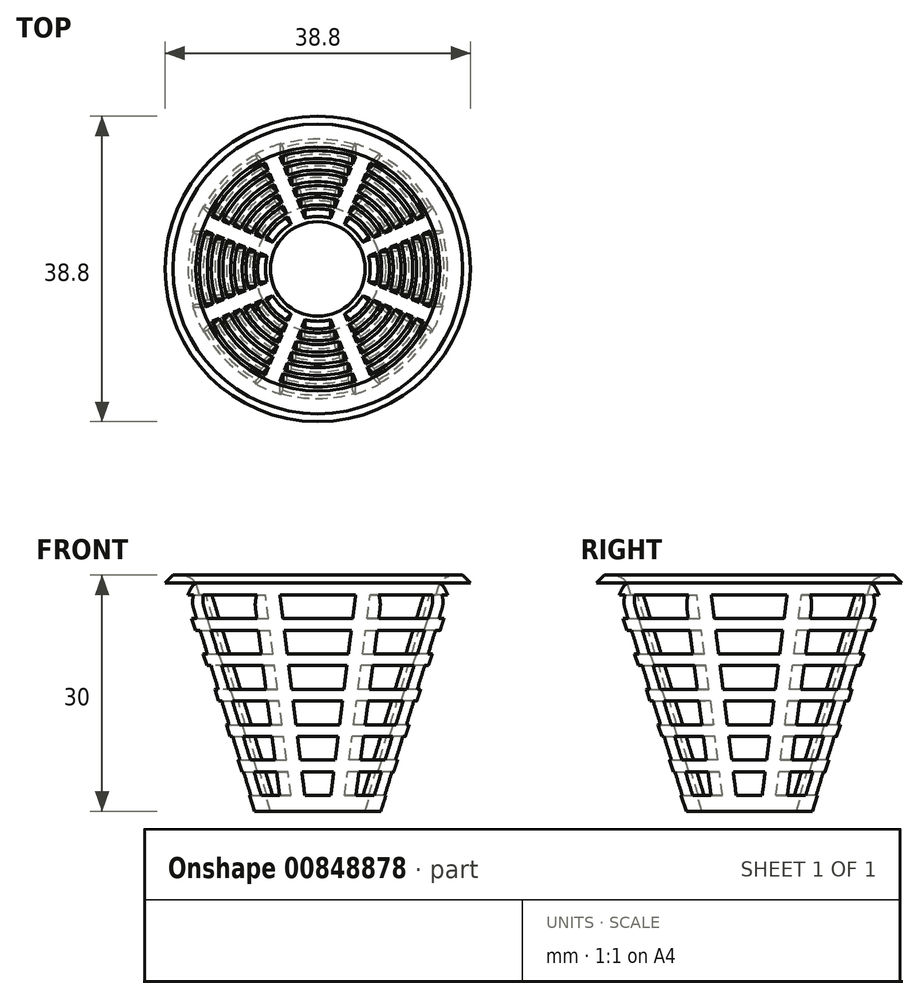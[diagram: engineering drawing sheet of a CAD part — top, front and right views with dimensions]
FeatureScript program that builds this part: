
annotation { "Feature Type Name" : "Feature", "Feature Type Description" : "" }
export const myFeature = defineFeature(function(context is Context, id is Id, definition is map)
    precondition{}
    {
        {
            var Q0;
            Q0=qCreatedBy(makeId("Top.planeOp"),FACE);
            var sketch = newSketch(context, id + "F0", { "sketchPlane" : qUnion([Q0])});
            skCircle(sketch, "E0", {"center": v(0, 0) * mm, "radius": 20 * mm});
            skCircle(sketch, "E1", {"center": v(0, 0) * mm, "radius": 24 * mm});
            skCircle(sketch, "E2", {"center": v(0, 0) * mm, "radius": 21 * mm});
            skCircle(sketch, "E3", {"center": v(0, 24) * mm, "radius": 1 * mm});
            skCircle(sketch, "E4.1.0", {"center": v(-3.75, 23.7) * mm, "radius": 1 * mm});
            skCircle(sketch, "E4.2.0", {"center": v(-7.42, 22.83) * mm, "radius": 1 * mm});
            skCircle(sketch, "E4.3.0", {"center": v(-10.9, 21.38) * mm, "radius": 1 * mm});
            skCircle(sketch, "E4.4.0", {"center": v(-14.1, 19.42) * mm, "radius": 1 * mm});
            skCircle(sketch, "E4.5.0", {"center": v(-16.97, 16.97) * mm, "radius": 1 * mm});
            skCircle(sketch, "E4.6.0", {"center": v(-19.42, 14.1) * mm, "radius": 1 * mm});
            skCircle(sketch, "E4.7.0", {"center": v(-21.38, 10.9) * mm, "radius": 1 * mm});
            skCircle(sketch, "E4.8.0", {"center": v(-22.83, 7.42) * mm, "radius": 1 * mm});
            skCircle(sketch, "E4.9.0", {"center": v(-23.7, 3.75) * mm, "radius": 1 * mm});
            skCircle(sketch, "E4.10.0", {"center": v(-24, 0) * mm, "radius": 1 * mm});
            skCircle(sketch, "E4.11.0", {"center": v(-23.7, -3.75) * mm, "radius": 1 * mm});
            skCircle(sketch, "E4.12.0", {"center": v(-22.83, -7.42) * mm, "radius": 1 * mm});
            skCircle(sketch, "E4.13.0", {"center": v(-21.38, -10.9) * mm, "radius": 1 * mm});
            skCircle(sketch, "E4.14.0", {"center": v(-19.42, -14.1) * mm, "radius": 1 * mm});
            skCircle(sketch, "E4.15.0", {"center": v(-16.97, -16.97) * mm, "radius": 1 * mm});
            skCircle(sketch, "E4.16.0", {"center": v(-14.1, -19.42) * mm, "radius": 1 * mm});
            skCircle(sketch, "E4.17.0", {"center": v(-10.9, -21.38) * mm, "radius": 1 * mm});
            skCircle(sketch, "E4.18.0", {"center": v(-7.42, -22.83) * mm, "radius": 1 * mm});
            skCircle(sketch, "E4.19.0", {"center": v(-3.75, -23.7) * mm, "radius": 1 * mm});
            skCircle(sketch, "E4.20.0", {"center": v(0, -24) * mm, "radius": 1 * mm});
            skCircle(sketch, "E4.21.0", {"center": v(3.75, -23.7) * mm, "radius": 1 * mm});
            skCircle(sketch, "E4.22.0", {"center": v(7.42, -22.83) * mm, "radius": 1 * mm});
            skCircle(sketch, "E4.23.0", {"center": v(10.9, -21.38) * mm, "radius": 1 * mm});
            skCircle(sketch, "E4.24.0", {"center": v(14.1, -19.42) * mm, "radius": 1 * mm});
            skCircle(sketch, "E4.25.0", {"center": v(16.97, -16.97) * mm, "radius": 1 * mm});
            skCircle(sketch, "E4.26.0", {"center": v(19.42, -14.1) * mm, "radius": 1 * mm});
            skCircle(sketch, "E4.27.0", {"center": v(21.38, -10.9) * mm, "radius": 1 * mm});
            skCircle(sketch, "E4.28.0", {"center": v(22.83, -7.42) * mm, "radius": 1 * mm});
            skCircle(sketch, "E4.29.0", {"center": v(23.7, -3.75) * mm, "radius": 1 * mm});
            skCircle(sketch, "E4.30.0", {"center": v(24, 0) * mm, "radius": 1 * mm});
            skCircle(sketch, "E4.31.0", {"center": v(23.7, 3.75) * mm, "radius": 1 * mm});
            skCircle(sketch, "E4.32.0", {"center": v(22.83, 7.42) * mm, "radius": 1 * mm});
            skCircle(sketch, "E4.33.0", {"center": v(21.38, 10.9) * mm, "radius": 1 * mm});
            skCircle(sketch, "E4.34.0", {"center": v(19.42, 14.1) * mm, "radius": 1 * mm});
            skCircle(sketch, "E4.35.0", {"center": v(16.97, 16.97) * mm, "radius": 1 * mm});
            skCircle(sketch, "E4.36.0", {"center": v(14.1, 19.42) * mm, "radius": 1 * mm});
            skCircle(sketch, "E4.37.0", {"center": v(10.9, 21.38) * mm, "radius": 1 * mm});
            skCircle(sketch, "E4.38.0", {"center": v(7.42, 22.83) * mm, "radius": 1 * mm});
            skCircle(sketch, "E4.39.0", {"center": v(3.75, 23.7) * mm, "radius": 1 * mm});
            skCircle(sketch, "E5", {"center": v(0, 0) * mm, "radius": 15.5 * mm});
            skCircle(sketch, "E6", {"center": v(0, 0) * mm, "radius": 17.5 * mm});
            skCircle(sketch, "E7", {"center": v(0, 0) * mm, "radius": 19.5 * mm});
            skSolve(sketch);
        }
        {
            var Q0;
            Q0=makeQuery(id+"F0.imprint","IMPRINT",FACE,{"disambiguationData":[TD([[makeQuery(id+"F0.imprint","IMPRINT",EDGE,{"derivedFrom":sQuery(id+"F0.wireOp",EDGE,"E6")}),-1.0]])]});
            var Q1;
            Q1=makeQuery(id+"F0.imprint","IMPRINT",FACE,{"disambiguationData":[TD([[makeQuery(id+"F0.imprint","IMPRINT",EDGE,{"derivedFrom":sQuery(id+"F0.wireOp",EDGE,"E5")}),-1.0]])]});
            extrude(context, id + "F1", {"entities" : qUnion([Q0, Q1]), "oppositeDirection" : true, "depth" : 1 * mm, "offsetDistance" : 25 * mm});
        }
        {
            var Q0;
            Q0=qCreatedBy(makeId("Top.planeOp"),FACE);
            cPlane(context, id + "F2", {"entities" : qUnion([Q0]), "cplaneType" : CPlaneType.OFFSET, "offset" : 30 * mm, "oppositeDirection" : true, "width" : 150 * mm, "height" : 150 * mm});
        }
        {
            var Q0;
            Q0=qCreatedBy(makeId("Front.planeOp"),FACE);
            var sketch = newSketch(context, id + "F3", { "sketchPlane" : qUnion([Q0])});
            skLineSegment(sketch, "E8", {"start": v(-8, -30) * mm, "end": v(-17.5, -1) * mm});
            skLineSegment(sketch, "E9", {"start": v(-17.5, -1) * mm, "end": v(-15.5, -1) * mm});
            skLineSegment(sketch, "E10", {"start": v(-15.5, -1) * mm, "end": v(-6, -30) * mm});
            skLineSegment(sketch, "E11", {"start": v(-6, -30) * mm, "end": v(-8, -30) * mm});
            skLineSegment(sketch, "E12", {"start": v(0, 0) * mm, "end": v(0, -30) * mm, "construction": true});
            skSolve(sketch);
        }
        {
            var Q0;
            Q0=makeQuery(id+"F3.imprint","IMPRINT",FACE,{"disambiguationData":[TD([[makeQuery(id+"F3.imprint","IMPRINT",EDGE,{"derivedFrom":sQuery(id+"F3.wireOp",EDGE,"E8")}),-1.0]])]});
            var Q1;
            Q1=sQuery(id+"F3.wireOp",EDGE,"E12");
            revolve(context, id + "F4", {"surfaceOperationType" : NewSurfaceOperationType.NEW, "entities" : qUnion([Q0]), "axis" : qUnion([Q1]), "revolveType" : RevolveType.FULL});
        }
        {
            var Q0;
            Q0=makeQuery(id+"F1.opExtrude","CAP_EDGE",EDGE,{"disambiguationData":[OSD([sQuery(id+"F0.wireOp",EDGE,"E5")])],"isStart":true});
            fillet(context, id + "F5", {"entities" : qUnion([Q0]), "radius" : 2.5 * mm, "tangentPropagation" : true, "allowEdgeOverflow" : false});
        }
        {
            var Q0;
            Q0=qCreatedBy(makeId("Front.planeOp"),FACE);
            var sketch = newSketch(context, id + "F6", { "sketchPlane" : qUnion([Q0])});
            skLineSegment(sketch, "E13", {"start": v(0, -30) * mm, "end": v(-1.4, -30) * mm});
            skLineSegment(sketch, "E14", {"start": v(0, -1) * mm, "end": v(-5, -1) * mm});
            skLineSegment(sketch, "E15", {"start": v(-5, -1) * mm, "end": v(-1.4, -30) * mm});
            skLineSegment(sketch, "E16.MirrorCS", {"start": v(5, -1) * mm, "end": v(1.4, -30) * mm});
            skLineSegment(sketch, "E17.MirrorCS", {"start": v(0, -1) * mm, "end": v(5, -1) * mm});
            skLineSegment(sketch, "E18.MirrorCS", {"start": v(0, -30) * mm, "end": v(1.4, -30) * mm});
            skLineSegment(sketch, "E19", {"start": v(-4.81, -2.5) * mm, "end": v(4.81, -2.5) * mm});
            skLineSegment(sketch, "E20.0.1.0", {"start": v(-4.63, -4) * mm, "end": v(4.63, -4) * mm});
            skLineSegment(sketch, "E20.0.2.0", {"start": v(-4.44, -5.5) * mm, "end": v(4.44, -5.5) * mm});
            skLineSegment(sketch, "E20.0.3.0", {"start": v(-4.26, -7) * mm, "end": v(4.26, -7) * mm});
            skLineSegment(sketch, "E20.0.4.0", {"start": v(-4.07, -8.5) * mm, "end": v(4.07, -8.5) * mm});
            skLineSegment(sketch, "E20.0.5.0", {"start": v(-3.88, -10) * mm, "end": v(3.88, -10) * mm});
            skLineSegment(sketch, "E20.0.6.0", {"start": v(-3.7, -11.5) * mm, "end": v(3.7, -11.5) * mm});
            skLineSegment(sketch, "E20.0.7.0", {"start": v(-3.51, -13) * mm, "end": v(3.51, -13) * mm});
            skLineSegment(sketch, "E20.0.8.0", {"start": v(-3.32, -14.5) * mm, "end": v(3.32, -14.5) * mm});
            skLineSegment(sketch, "E20.0.9.0", {"start": v(-3.14, -16) * mm, "end": v(3.14, -16) * mm});
            skLineSegment(sketch, "E20.0.10.0", {"start": v(-2.95, -17.5) * mm, "end": v(2.95, -17.5) * mm});
            skLineSegment(sketch, "E20.0.11.0", {"start": v(-2.77, -19) * mm, "end": v(2.77, -19) * mm});
            skLineSegment(sketch, "E20.0.12.0", {"start": v(-2.58, -20.5) * mm, "end": v(2.58, -20.5) * mm});
            skLineSegment(sketch, "E20.0.13.0", {"start": v(-2.4, -22) * mm, "end": v(2.4, -22) * mm});
            skLineSegment(sketch, "E20.0.14.0", {"start": v(-2.2, -23.5) * mm, "end": v(2.2, -23.5) * mm});
            skLineSegment(sketch, "E20.0.15.0", {"start": v(-2.02, -25) * mm, "end": v(2.02, -25) * mm});
            skLineSegment(sketch, "E20.0.16.0", {"start": v(-1.83, -26.5) * mm, "end": v(1.83, -26.5) * mm});
            skLineSegment(sketch, "E20.0.17.0", {"start": v(-1.65, -28) * mm, "end": v(1.65, -28) * mm});
            skLineSegment(sketch, "E20.direction1", {"start": v(-4.81, -2.5) * mm, "end": v(20.18, -2.5) * mm, "construction": true});
            skLineSegment(sketch, "E20.direction2", {"start": v(-4.81, -2.5) * mm, "end": v(-4.81, -4) * mm, "construction": true});
            skPoint(sketch, "E21.orphan", {"position": v(-4.81, -7) * mm});
            skPoint(sketch, "E22.orphan", {"position": v(-4.81, -5.5) * mm});
            skPoint(sketch, "E23.orphan", {"position": v(-4.81, -8.5) * mm});
            skPoint(sketch, "E24.orphan", {"position": v(-4.81, -10) * mm});
            skPoint(sketch, "E25.orphan", {"position": v(-4.81, -11.5) * mm});
            skPoint(sketch, "E26.orphan", {"position": v(-4.81, -13) * mm});
            skPoint(sketch, "E27.orphan", {"position": v(-4.81, -14.5) * mm});
            skPoint(sketch, "E28.orphan", {"position": v(-4.81, -16) * mm});
            skPoint(sketch, "E29.orphan", {"position": v(-4.81, -17.5) * mm});
            skPoint(sketch, "E30.orphan", {"position": v(-4.81, -19) * mm});
            skPoint(sketch, "E31.orphan", {"position": v(-4.81, -20.5) * mm});
            skPoint(sketch, "E32.orphan", {"position": v(-4.81, -22) * mm});
            skPoint(sketch, "E33.orphan", {"position": v(-4.81, -23.5) * mm});
            skPoint(sketch, "E34.orphan", {"position": v(-4.81, -25) * mm});
            skPoint(sketch, "E35.orphan", {"position": v(-4.81, -26.5) * mm});
            skPoint(sketch, "E36.orphan", {"position": v(-4.81, -28) * mm});
            skPoint(sketch, "E37.orphan", {"position": v(4.81, -28) * mm});
            skPoint(sketch, "E38.orphan", {"position": v(4.81, -26.5) * mm});
            skPoint(sketch, "E39.orphan", {"position": v(4.81, -25) * mm});
            skPoint(sketch, "E40.orphan", {"position": v(4.81, -23.5) * mm});
            skPoint(sketch, "E41.orphan", {"position": v(4.81, -22) * mm});
            skPoint(sketch, "E42.orphan", {"position": v(4.81, -20.5) * mm});
            skPoint(sketch, "E43.orphan", {"position": v(4.81, -19) * mm});
            skPoint(sketch, "E44.orphan", {"position": v(4.81, -17.5) * mm});
            skPoint(sketch, "E45.orphan", {"position": v(4.81, -16) * mm});
            skPoint(sketch, "E46.orphan", {"position": v(4.81, -14.5) * mm});
            skPoint(sketch, "E47.orphan", {"position": v(4.81, -13) * mm});
            skPoint(sketch, "E48.orphan", {"position": v(4.81, -11.5) * mm});
            skPoint(sketch, "E49.orphan", {"position": v(4.81, -10) * mm});
            skPoint(sketch, "E50.orphan", {"position": v(4.81, -8.5) * mm});
            skPoint(sketch, "E51.orphan", {"position": v(4.81, -7) * mm});
            skPoint(sketch, "E52.orphan", {"position": v(4.81, -5.5) * mm});
            skPoint(sketch, "E53.orphan", {"position": v(4.81, -4) * mm});
            skSolve(sketch);
        }
        {
            var Q0;
            {var subQ0=sQuery(id+"F6.wireOp",EDGE,"E19");Q0=makeQuery(id+"F6.imprint","IMPRINT",FACE,{"disambiguationData":[TD([[makeQuery(id+"F6.imprint","IMPRINT",EDGE,{"derivedFrom":subQ0}),-1.0]])]});}
            var Q1;
            {var subQ0=sQuery(id+"F6.wireOp",EDGE,"E20.0.1.0");Q1=makeQuery(id+"F6.imprint","IMPRINT",FACE,{"disambiguationData":[TD([[makeQuery(id+"F6.imprint","IMPRINT",EDGE,{"derivedFrom":subQ0}),-1.0]])]});}
            var Q2;
            {var subQ0=sQuery(id+"F6.wireOp",EDGE,"E20.0.4.0");Q2=makeQuery(id+"F6.imprint","IMPRINT",FACE,{"disambiguationData":[TD([[makeQuery(id+"F6.imprint","IMPRINT",EDGE,{"derivedFrom":subQ0}),-1.0]])]});}
            var Q3;
            {var subQ0=sQuery(id+"F6.wireOp",EDGE,"E20.0.7.0");Q3=makeQuery(id+"F6.imprint","IMPRINT",FACE,{"disambiguationData":[TD([[makeQuery(id+"F6.imprint","IMPRINT",EDGE,{"derivedFrom":subQ0}),-1.0]])]});}
            var Q4;
            {var subQ0=sQuery(id+"F6.wireOp",EDGE,"E20.0.10.0");Q4=makeQuery(id+"F6.imprint","IMPRINT",FACE,{"disambiguationData":[TD([[makeQuery(id+"F6.imprint","IMPRINT",EDGE,{"derivedFrom":subQ0}),-1.0]])]});}
            var Q5;
            {var subQ0=sQuery(id+"F6.wireOp",EDGE,"E20.0.13.0");Q5=makeQuery(id+"F6.imprint","IMPRINT",FACE,{"disambiguationData":[TD([[makeQuery(id+"F6.imprint","IMPRINT",EDGE,{"derivedFrom":subQ0}),-1.0]])]});}
            var Q6;
            {var subQ0=sQuery(id+"F6.wireOp",EDGE,"E20.0.3.0");Q6=makeQuery(id+"F6.imprint","IMPRINT",FACE,{"disambiguationData":[TD([[makeQuery(id+"F6.imprint","IMPRINT",EDGE,{"derivedFrom":subQ0}),-1.0]])]});}
            var Q7;
            {var subQ0=sQuery(id+"F6.wireOp",EDGE,"E20.0.6.0");Q7=makeQuery(id+"F6.imprint","IMPRINT",FACE,{"disambiguationData":[TD([[makeQuery(id+"F6.imprint","IMPRINT",EDGE,{"derivedFrom":subQ0}),-1.0]])]});}
            var Q8;
            {var subQ0=sQuery(id+"F6.wireOp",EDGE,"E20.0.9.0");Q8=makeQuery(id+"F6.imprint","IMPRINT",FACE,{"disambiguationData":[TD([[makeQuery(id+"F6.imprint","IMPRINT",EDGE,{"derivedFrom":subQ0}),-1.0]])]});}
            var Q9;
            {var subQ0=sQuery(id+"F6.wireOp",EDGE,"E20.0.12.0");Q9=makeQuery(id+"F6.imprint","IMPRINT",FACE,{"disambiguationData":[TD([[makeQuery(id+"F6.imprint","IMPRINT",EDGE,{"derivedFrom":subQ0}),-1.0]])]});}
            var Q10;
            {var subQ0=sQuery(id+"F6.wireOp",EDGE,"E20.0.15.0");Q10=makeQuery(id+"F6.imprint","IMPRINT",FACE,{"disambiguationData":[TD([[makeQuery(id+"F6.imprint","IMPRINT",EDGE,{"derivedFrom":subQ0}),-1.0]])]});}
            var Q11;
            {var subQ0=sQuery(id+"F6.wireOp",EDGE,"E20.0.16.0");Q11=makeQuery(id+"F6.imprint","IMPRINT",FACE,{"disambiguationData":[TD([[makeQuery(id+"F6.imprint","IMPRINT",EDGE,{"derivedFrom":subQ0}),-1.0]])]});}
            extrude(context, id + "F7", {"entities" : qUnion([Q0, Q1, Q2, Q3, Q4, Q5, Q6, Q7, Q8, Q9, Q10, Q11]), "depth" : 25 * mm, "offsetDistance" : 25 * mm});
        }
        {
            var Q0;
            Q0=makeQuery(id+"F7.opExtrude","SWEPT_BODY",BODY,{"disambiguationData":[OSD([sQuery(id+"F6.wireOp",EDGE,"E15"),sQuery(id+"F6.wireOp",EDGE,"E16.MirrorCS"),sQuery(id+"F6.wireOp",EDGE,"E20.0.6.0"),sQuery(id+"F6.wireOp",EDGE,"E20.0.7.0")])]});
            var Q1;
            Q1=makeQuery(id+"F7.opExtrude","SWEPT_BODY",BODY,{"disambiguationData":[OSD([sQuery(id+"F6.wireOp",EDGE,"E15"),sQuery(id+"F6.wireOp",EDGE,"E16.MirrorCS"),sQuery(id+"F6.wireOp",EDGE,"E20.0.16.0"),sQuery(id+"F6.wireOp",EDGE,"E20.0.17.0")])]});
            var Q2;
            Q2=makeQuery(id+"F7.opExtrude","SWEPT_BODY",BODY,{"disambiguationData":[OSD([sQuery(id+"F6.wireOp",EDGE,"E15"),sQuery(id+"F6.wireOp",EDGE,"E16.MirrorCS"),sQuery(id+"F6.wireOp",EDGE,"E19"),sQuery(id+"F6.wireOp",EDGE,"E20.0.1.0")])]});
            var Q3;
            Q3=makeQuery(id+"F7.opExtrude","SWEPT_BODY",BODY,{"disambiguationData":[OSD([sQuery(id+"F6.wireOp",EDGE,"E15"),sQuery(id+"F6.wireOp",EDGE,"E16.MirrorCS"),sQuery(id+"F6.wireOp",EDGE,"E20.0.4.0"),sQuery(id+"F6.wireOp",EDGE,"E20.0.5.0")])]});
            var Q4;
            Q4=makeQuery(id+"F7.opExtrude","SWEPT_BODY",BODY,{"disambiguationData":[OSD([sQuery(id+"F6.wireOp",EDGE,"E15"),sQuery(id+"F6.wireOp",EDGE,"E16.MirrorCS"),sQuery(id+"F6.wireOp",EDGE,"E20.0.14.0"),sQuery(id+"F6.wireOp",EDGE,"E20.0.15.0")])]});
            var Q5;
            Q5=makeQuery(id+"F7.opExtrude","SWEPT_BODY",BODY,{"disambiguationData":[OSD([sQuery(id+"F6.wireOp",EDGE,"E15"),sQuery(id+"F6.wireOp",EDGE,"E16.MirrorCS"),sQuery(id+"F6.wireOp",EDGE,"E20.0.12.0"),sQuery(id+"F6.wireOp",EDGE,"E20.0.13.0")])]});
            var Q6;
            Q6=makeQuery(id+"F7.opExtrude","SWEPT_BODY",BODY,{"disambiguationData":[OSD([sQuery(id+"F6.wireOp",EDGE,"E15"),sQuery(id+"F6.wireOp",EDGE,"E16.MirrorCS"),sQuery(id+"F6.wireOp",EDGE,"E20.0.10.0"),sQuery(id+"F6.wireOp",EDGE,"E20.0.11.0")])]});
            var Q7;
            Q7=makeQuery(id+"F7.opExtrude","SWEPT_BODY",BODY,{"disambiguationData":[OSD([sQuery(id+"F6.wireOp",EDGE,"E15"),sQuery(id+"F6.wireOp",EDGE,"E16.MirrorCS"),sQuery(id+"F6.wireOp",EDGE,"E20.0.2.0"),sQuery(id+"F6.wireOp",EDGE,"E20.0.3.0")])]});
            var Q8;
            Q8=makeQuery(id+"F7.opExtrude","SWEPT_BODY",BODY,{"disambiguationData":[OSD([sQuery(id+"F6.wireOp",EDGE,"E15"),sQuery(id+"F6.wireOp",EDGE,"E16.MirrorCS"),sQuery(id+"F6.wireOp",EDGE,"E20.0.8.0"),sQuery(id+"F6.wireOp",EDGE,"E20.0.9.0")])]});
            var Q9;
            Q9=sQuery(id+"F3.wireOp",EDGE,"E12");
            circularPattern(context, id + "F8", {"entities" : qUnion([Q0, Q1, Q2, Q3, Q4, Q5, Q6, Q7, Q8]), "axis" : qUnion([Q9]), "angle" : 360 * degree, "instanceCount" : 8, "equalSpace" : true});
        }
        {
            var Q0;
            Q0=makeQuery(id+"F8.opPattern","COPY",BODY,{"derivedFrom":makeQuery(id+"F7.opExtrude","SWEPT_BODY",BODY,{"disambiguationData":[OSD([sQuery(id+"F6.wireOp",EDGE,"E15"),sQuery(id+"F6.wireOp",EDGE,"E16.MirrorCS"),sQuery(id+"F6.wireOp",EDGE,"E20.0.4.0"),sQuery(id+"F6.wireOp",EDGE,"E20.0.5.0")])]}),"instanceName":"2"});
            var Q1;
            Q1=makeQuery(id+"F8.opPattern","COPY",BODY,{"derivedFrom":makeQuery(id+"F7.opExtrude","SWEPT_BODY",BODY,{"disambiguationData":[OSD([sQuery(id+"F6.wireOp",EDGE,"E15"),sQuery(id+"F6.wireOp",EDGE,"E16.MirrorCS"),sQuery(id+"F6.wireOp",EDGE,"E20.0.6.0"),sQuery(id+"F6.wireOp",EDGE,"E20.0.7.0")])]}),"instanceName":"7"});
            var Q2;
            Q2=makeQuery(id+"F8.opPattern","COPY",BODY,{"derivedFrom":makeQuery(id+"F7.opExtrude","SWEPT_BODY",BODY,{"disambiguationData":[OSD([sQuery(id+"F6.wireOp",EDGE,"E15"),sQuery(id+"F6.wireOp",EDGE,"E16.MirrorCS"),sQuery(id+"F6.wireOp",EDGE,"E20.0.16.0"),sQuery(id+"F6.wireOp",EDGE,"E20.0.17.0")])]}),"instanceName":"7"});
            var Q3;
            Q3=makeQuery(id+"F8.opPattern","COPY",BODY,{"derivedFrom":makeQuery(id+"F7.opExtrude","SWEPT_BODY",BODY,{"disambiguationData":[OSD([sQuery(id+"F6.wireOp",EDGE,"E15"),sQuery(id+"F6.wireOp",EDGE,"E16.MirrorCS"),sQuery(id+"F6.wireOp",EDGE,"E20.0.10.0"),sQuery(id+"F6.wireOp",EDGE,"E20.0.11.0")])]}),"instanceName":"1"});
            var Q4;
            Q4=makeQuery(id+"F8.opPattern","COPY",BODY,{"derivedFrom":makeQuery(id+"F7.opExtrude","SWEPT_BODY",BODY,{"disambiguationData":[OSD([sQuery(id+"F6.wireOp",EDGE,"E15"),sQuery(id+"F6.wireOp",EDGE,"E16.MirrorCS"),sQuery(id+"F6.wireOp",EDGE,"E19"),sQuery(id+"F6.wireOp",EDGE,"E20.0.1.0")])]}),"instanceName":"7"});
            var Q5;
            Q5=makeQuery(id+"F8.opPattern","COPY",BODY,{"derivedFrom":makeQuery(id+"F7.opExtrude","SWEPT_BODY",BODY,{"disambiguationData":[OSD([sQuery(id+"F6.wireOp",EDGE,"E15"),sQuery(id+"F6.wireOp",EDGE,"E16.MirrorCS"),sQuery(id+"F6.wireOp",EDGE,"E20.0.12.0"),sQuery(id+"F6.wireOp",EDGE,"E20.0.13.0")])]}),"instanceName":"1"});
            var Q6;
            Q6=makeQuery(id+"F8.opPattern","COPY",BODY,{"derivedFrom":makeQuery(id+"F7.opExtrude","SWEPT_BODY",BODY,{"disambiguationData":[OSD([sQuery(id+"F6.wireOp",EDGE,"E15"),sQuery(id+"F6.wireOp",EDGE,"E16.MirrorCS"),sQuery(id+"F6.wireOp",EDGE,"E20.0.14.0"),sQuery(id+"F6.wireOp",EDGE,"E20.0.15.0")])]}),"instanceName":"1"});
            var Q7;
            Q7=makeQuery(id+"F8.opPattern","COPY",BODY,{"derivedFrom":makeQuery(id+"F7.opExtrude","SWEPT_BODY",BODY,{"disambiguationData":[OSD([sQuery(id+"F6.wireOp",EDGE,"E15"),sQuery(id+"F6.wireOp",EDGE,"E16.MirrorCS"),sQuery(id+"F6.wireOp",EDGE,"E20.0.16.0"),sQuery(id+"F6.wireOp",EDGE,"E20.0.17.0")])]}),"instanceName":"1"});
            var Q8;
            Q8=makeQuery(id+"F8.opPattern","COPY",BODY,{"derivedFrom":makeQuery(id+"F7.opExtrude","SWEPT_BODY",BODY,{"disambiguationData":[OSD([sQuery(id+"F6.wireOp",EDGE,"E15"),sQuery(id+"F6.wireOp",EDGE,"E16.MirrorCS"),sQuery(id+"F6.wireOp",EDGE,"E19"),sQuery(id+"F6.wireOp",EDGE,"E20.0.1.0")])]}),"instanceName":"2"});
            var Q9;
            Q9=makeQuery(id+"F8.opPattern","COPY",BODY,{"derivedFrom":makeQuery(id+"F7.opExtrude","SWEPT_BODY",BODY,{"disambiguationData":[OSD([sQuery(id+"F6.wireOp",EDGE,"E15"),sQuery(id+"F6.wireOp",EDGE,"E16.MirrorCS"),sQuery(id+"F6.wireOp",EDGE,"E20.0.2.0"),sQuery(id+"F6.wireOp",EDGE,"E20.0.3.0")])]}),"instanceName":"2"});
            var Q10;
            Q10=makeQuery(id+"F8.opPattern","COPY",BODY,{"derivedFrom":makeQuery(id+"F7.opExtrude","SWEPT_BODY",BODY,{"disambiguationData":[OSD([sQuery(id+"F6.wireOp",EDGE,"E15"),sQuery(id+"F6.wireOp",EDGE,"E16.MirrorCS"),sQuery(id+"F6.wireOp",EDGE,"E20.0.4.0"),sQuery(id+"F6.wireOp",EDGE,"E20.0.5.0")])]}),"instanceName":"1"});
            var Q11;
            Q11=makeQuery(id+"F8.opPattern","COPY",BODY,{"derivedFrom":makeQuery(id+"F7.opExtrude","SWEPT_BODY",BODY,{"disambiguationData":[OSD([sQuery(id+"F6.wireOp",EDGE,"E15"),sQuery(id+"F6.wireOp",EDGE,"E16.MirrorCS"),sQuery(id+"F6.wireOp",EDGE,"E20.0.2.0"),sQuery(id+"F6.wireOp",EDGE,"E20.0.3.0")])]}),"instanceName":"1"});
            var Q12;
            Q12=makeQuery(id+"F8.opPattern","COPY",BODY,{"derivedFrom":makeQuery(id+"F7.opExtrude","SWEPT_BODY",BODY,{"disambiguationData":[OSD([sQuery(id+"F6.wireOp",EDGE,"E15"),sQuery(id+"F6.wireOp",EDGE,"E16.MirrorCS"),sQuery(id+"F6.wireOp",EDGE,"E19"),sQuery(id+"F6.wireOp",EDGE,"E20.0.1.0")])]}),"instanceName":"1"});
            var Q13;
            Q13=makeQuery(id+"F7.opExtrude","SWEPT_BODY",BODY,{"disambiguationData":[OSD([sQuery(id+"F6.wireOp",EDGE,"E15"),sQuery(id+"F6.wireOp",EDGE,"E16.MirrorCS"),sQuery(id+"F6.wireOp",EDGE,"E20.0.16.0"),sQuery(id+"F6.wireOp",EDGE,"E20.0.17.0")])]});
            var Q14;
            Q14=makeQuery(id+"F7.opExtrude","SWEPT_BODY",BODY,{"disambiguationData":[OSD([sQuery(id+"F6.wireOp",EDGE,"E15"),sQuery(id+"F6.wireOp",EDGE,"E16.MirrorCS"),sQuery(id+"F6.wireOp",EDGE,"E20.0.14.0"),sQuery(id+"F6.wireOp",EDGE,"E20.0.15.0")])]});
            var Q15;
            Q15=makeQuery(id+"F7.opExtrude","SWEPT_BODY",BODY,{"disambiguationData":[OSD([sQuery(id+"F6.wireOp",EDGE,"E15"),sQuery(id+"F6.wireOp",EDGE,"E16.MirrorCS"),sQuery(id+"F6.wireOp",EDGE,"E20.0.12.0"),sQuery(id+"F6.wireOp",EDGE,"E20.0.13.0")])]});
            var Q16;
            Q16=makeQuery(id+"F8.opPattern","COPY",BODY,{"derivedFrom":makeQuery(id+"F7.opExtrude","SWEPT_BODY",BODY,{"disambiguationData":[OSD([sQuery(id+"F6.wireOp",EDGE,"E15"),sQuery(id+"F6.wireOp",EDGE,"E16.MirrorCS"),sQuery(id+"F6.wireOp",EDGE,"E20.0.14.0"),sQuery(id+"F6.wireOp",EDGE,"E20.0.15.0")])]}),"instanceName":"6"});
            var Q17;
            Q17=makeQuery(id+"F7.opExtrude","SWEPT_BODY",BODY,{"disambiguationData":[OSD([sQuery(id+"F6.wireOp",EDGE,"E15"),sQuery(id+"F6.wireOp",EDGE,"E16.MirrorCS"),sQuery(id+"F6.wireOp",EDGE,"E20.0.2.0"),sQuery(id+"F6.wireOp",EDGE,"E20.0.3.0")])]});
            var Q18;
            Q18=makeQuery(id+"F8.opPattern","COPY",BODY,{"derivedFrom":makeQuery(id+"F7.opExtrude","SWEPT_BODY",BODY,{"disambiguationData":[OSD([sQuery(id+"F6.wireOp",EDGE,"E15"),sQuery(id+"F6.wireOp",EDGE,"E16.MirrorCS"),sQuery(id+"F6.wireOp",EDGE,"E20.0.8.0"),sQuery(id+"F6.wireOp",EDGE,"E20.0.9.0")])]}),"instanceName":"1"});
            var Q19;
            Q19=makeQuery(id+"F8.opPattern","COPY",BODY,{"derivedFrom":makeQuery(id+"F7.opExtrude","SWEPT_BODY",BODY,{"disambiguationData":[OSD([sQuery(id+"F6.wireOp",EDGE,"E15"),sQuery(id+"F6.wireOp",EDGE,"E16.MirrorCS"),sQuery(id+"F6.wireOp",EDGE,"E20.0.4.0"),sQuery(id+"F6.wireOp",EDGE,"E20.0.5.0")])]}),"instanceName":"7"});
            var Q20;
            Q20=makeQuery(id+"F8.opPattern","COPY",BODY,{"derivedFrom":makeQuery(id+"F7.opExtrude","SWEPT_BODY",BODY,{"disambiguationData":[OSD([sQuery(id+"F6.wireOp",EDGE,"E15"),sQuery(id+"F6.wireOp",EDGE,"E16.MirrorCS"),sQuery(id+"F6.wireOp",EDGE,"E20.0.12.0"),sQuery(id+"F6.wireOp",EDGE,"E20.0.13.0")])]}),"instanceName":"6"});
            var Q21;
            Q21=makeQuery(id+"F8.opPattern","COPY",BODY,{"derivedFrom":makeQuery(id+"F7.opExtrude","SWEPT_BODY",BODY,{"disambiguationData":[OSD([sQuery(id+"F6.wireOp",EDGE,"E15"),sQuery(id+"F6.wireOp",EDGE,"E16.MirrorCS"),sQuery(id+"F6.wireOp",EDGE,"E20.0.16.0"),sQuery(id+"F6.wireOp",EDGE,"E20.0.17.0")])]}),"instanceName":"6"});
            var Q22;
            Q22=makeQuery(id+"F8.opPattern","COPY",BODY,{"derivedFrom":makeQuery(id+"F7.opExtrude","SWEPT_BODY",BODY,{"disambiguationData":[OSD([sQuery(id+"F6.wireOp",EDGE,"E15"),sQuery(id+"F6.wireOp",EDGE,"E16.MirrorCS"),sQuery(id+"F6.wireOp",EDGE,"E20.0.10.0"),sQuery(id+"F6.wireOp",EDGE,"E20.0.11.0")])]}),"instanceName":"6"});
            var Q23;
            Q23=makeQuery(id+"F8.opPattern","COPY",BODY,{"derivedFrom":makeQuery(id+"F7.opExtrude","SWEPT_BODY",BODY,{"disambiguationData":[OSD([sQuery(id+"F6.wireOp",EDGE,"E15"),sQuery(id+"F6.wireOp",EDGE,"E16.MirrorCS"),sQuery(id+"F6.wireOp",EDGE,"E20.0.8.0"),sQuery(id+"F6.wireOp",EDGE,"E20.0.9.0")])]}),"instanceName":"6"});
            var Q24;
            Q24=makeQuery(id+"F8.opPattern","COPY",BODY,{"derivedFrom":makeQuery(id+"F7.opExtrude","SWEPT_BODY",BODY,{"disambiguationData":[OSD([sQuery(id+"F6.wireOp",EDGE,"E15"),sQuery(id+"F6.wireOp",EDGE,"E16.MirrorCS"),sQuery(id+"F6.wireOp",EDGE,"E20.0.6.0"),sQuery(id+"F6.wireOp",EDGE,"E20.0.7.0")])]}),"instanceName":"6"});
            var Q25;
            Q25=makeQuery(id+"F8.opPattern","COPY",BODY,{"derivedFrom":makeQuery(id+"F7.opExtrude","SWEPT_BODY",BODY,{"disambiguationData":[OSD([sQuery(id+"F6.wireOp",EDGE,"E15"),sQuery(id+"F6.wireOp",EDGE,"E16.MirrorCS"),sQuery(id+"F6.wireOp",EDGE,"E20.0.4.0"),sQuery(id+"F6.wireOp",EDGE,"E20.0.5.0")])]}),"instanceName":"6"});
            var Q26;
            Q26=makeQuery(id+"F8.opPattern","COPY",BODY,{"derivedFrom":makeQuery(id+"F7.opExtrude","SWEPT_BODY",BODY,{"disambiguationData":[OSD([sQuery(id+"F6.wireOp",EDGE,"E15"),sQuery(id+"F6.wireOp",EDGE,"E16.MirrorCS"),sQuery(id+"F6.wireOp",EDGE,"E20.0.2.0"),sQuery(id+"F6.wireOp",EDGE,"E20.0.3.0")])]}),"instanceName":"6"});
            var Q27;
            Q27=makeQuery(id+"F8.opPattern","COPY",BODY,{"derivedFrom":makeQuery(id+"F7.opExtrude","SWEPT_BODY",BODY,{"disambiguationData":[OSD([sQuery(id+"F6.wireOp",EDGE,"E15"),sQuery(id+"F6.wireOp",EDGE,"E16.MirrorCS"),sQuery(id+"F6.wireOp",EDGE,"E19"),sQuery(id+"F6.wireOp",EDGE,"E20.0.1.0")])]}),"instanceName":"6"});
            var Q28;
            Q28=makeQuery(id+"F8.opPattern","COPY",BODY,{"derivedFrom":makeQuery(id+"F7.opExtrude","SWEPT_BODY",BODY,{"disambiguationData":[OSD([sQuery(id+"F6.wireOp",EDGE,"E15"),sQuery(id+"F6.wireOp",EDGE,"E16.MirrorCS"),sQuery(id+"F6.wireOp",EDGE,"E20.0.16.0"),sQuery(id+"F6.wireOp",EDGE,"E20.0.17.0")])]}),"instanceName":"5"});
            var Q29;
            Q29=makeQuery(id+"F8.opPattern","COPY",BODY,{"derivedFrom":makeQuery(id+"F7.opExtrude","SWEPT_BODY",BODY,{"disambiguationData":[OSD([sQuery(id+"F6.wireOp",EDGE,"E15"),sQuery(id+"F6.wireOp",EDGE,"E16.MirrorCS"),sQuery(id+"F6.wireOp",EDGE,"E20.0.14.0"),sQuery(id+"F6.wireOp",EDGE,"E20.0.15.0")])]}),"instanceName":"5"});
            var Q30;
            Q30=makeQuery(id+"F8.opPattern","COPY",BODY,{"derivedFrom":makeQuery(id+"F7.opExtrude","SWEPT_BODY",BODY,{"disambiguationData":[OSD([sQuery(id+"F6.wireOp",EDGE,"E15"),sQuery(id+"F6.wireOp",EDGE,"E16.MirrorCS"),sQuery(id+"F6.wireOp",EDGE,"E20.0.12.0"),sQuery(id+"F6.wireOp",EDGE,"E20.0.13.0")])]}),"instanceName":"5"});
            var Q31;
            Q31=makeQuery(id+"F8.opPattern","COPY",BODY,{"derivedFrom":makeQuery(id+"F7.opExtrude","SWEPT_BODY",BODY,{"disambiguationData":[OSD([sQuery(id+"F6.wireOp",EDGE,"E15"),sQuery(id+"F6.wireOp",EDGE,"E16.MirrorCS"),sQuery(id+"F6.wireOp",EDGE,"E20.0.10.0"),sQuery(id+"F6.wireOp",EDGE,"E20.0.11.0")])]}),"instanceName":"5"});
            var Q32;
            Q32=makeQuery(id+"F8.opPattern","COPY",BODY,{"derivedFrom":makeQuery(id+"F7.opExtrude","SWEPT_BODY",BODY,{"disambiguationData":[OSD([sQuery(id+"F6.wireOp",EDGE,"E15"),sQuery(id+"F6.wireOp",EDGE,"E16.MirrorCS"),sQuery(id+"F6.wireOp",EDGE,"E20.0.8.0"),sQuery(id+"F6.wireOp",EDGE,"E20.0.9.0")])]}),"instanceName":"5"});
            var Q33;
            Q33=makeQuery(id+"F8.opPattern","COPY",BODY,{"derivedFrom":makeQuery(id+"F7.opExtrude","SWEPT_BODY",BODY,{"disambiguationData":[OSD([sQuery(id+"F6.wireOp",EDGE,"E15"),sQuery(id+"F6.wireOp",EDGE,"E16.MirrorCS"),sQuery(id+"F6.wireOp",EDGE,"E20.0.6.0"),sQuery(id+"F6.wireOp",EDGE,"E20.0.7.0")])]}),"instanceName":"5"});
            var Q34;
            Q34=makeQuery(id+"F8.opPattern","COPY",BODY,{"derivedFrom":makeQuery(id+"F7.opExtrude","SWEPT_BODY",BODY,{"disambiguationData":[OSD([sQuery(id+"F6.wireOp",EDGE,"E15"),sQuery(id+"F6.wireOp",EDGE,"E16.MirrorCS"),sQuery(id+"F6.wireOp",EDGE,"E20.0.4.0"),sQuery(id+"F6.wireOp",EDGE,"E20.0.5.0")])]}),"instanceName":"5"});
            var Q35;
            Q35=makeQuery(id+"F8.opPattern","COPY",BODY,{"derivedFrom":makeQuery(id+"F7.opExtrude","SWEPT_BODY",BODY,{"disambiguationData":[OSD([sQuery(id+"F6.wireOp",EDGE,"E15"),sQuery(id+"F6.wireOp",EDGE,"E16.MirrorCS"),sQuery(id+"F6.wireOp",EDGE,"E20.0.2.0"),sQuery(id+"F6.wireOp",EDGE,"E20.0.3.0")])]}),"instanceName":"5"});
            var Q36;
            Q36=makeQuery(id+"F8.opPattern","COPY",BODY,{"derivedFrom":makeQuery(id+"F7.opExtrude","SWEPT_BODY",BODY,{"disambiguationData":[OSD([sQuery(id+"F6.wireOp",EDGE,"E15"),sQuery(id+"F6.wireOp",EDGE,"E16.MirrorCS"),sQuery(id+"F6.wireOp",EDGE,"E19"),sQuery(id+"F6.wireOp",EDGE,"E20.0.1.0")])]}),"instanceName":"5"});
            var Q37;
            Q37=makeQuery(id+"F8.opPattern","COPY",BODY,{"derivedFrom":makeQuery(id+"F7.opExtrude","SWEPT_BODY",BODY,{"disambiguationData":[OSD([sQuery(id+"F6.wireOp",EDGE,"E15"),sQuery(id+"F6.wireOp",EDGE,"E16.MirrorCS"),sQuery(id+"F6.wireOp",EDGE,"E20.0.16.0"),sQuery(id+"F6.wireOp",EDGE,"E20.0.17.0")])]}),"instanceName":"4"});
            var Q38;
            Q38=makeQuery(id+"F8.opPattern","COPY",BODY,{"derivedFrom":makeQuery(id+"F7.opExtrude","SWEPT_BODY",BODY,{"disambiguationData":[OSD([sQuery(id+"F6.wireOp",EDGE,"E15"),sQuery(id+"F6.wireOp",EDGE,"E16.MirrorCS"),sQuery(id+"F6.wireOp",EDGE,"E20.0.14.0"),sQuery(id+"F6.wireOp",EDGE,"E20.0.15.0")])]}),"instanceName":"4"});
            var Q39;
            Q39=makeQuery(id+"F8.opPattern","COPY",BODY,{"derivedFrom":makeQuery(id+"F7.opExtrude","SWEPT_BODY",BODY,{"disambiguationData":[OSD([sQuery(id+"F6.wireOp",EDGE,"E15"),sQuery(id+"F6.wireOp",EDGE,"E16.MirrorCS"),sQuery(id+"F6.wireOp",EDGE,"E20.0.12.0"),sQuery(id+"F6.wireOp",EDGE,"E20.0.13.0")])]}),"instanceName":"4"});
            var Q40;
            Q40=makeQuery(id+"F8.opPattern","COPY",BODY,{"derivedFrom":makeQuery(id+"F7.opExtrude","SWEPT_BODY",BODY,{"disambiguationData":[OSD([sQuery(id+"F6.wireOp",EDGE,"E15"),sQuery(id+"F6.wireOp",EDGE,"E16.MirrorCS"),sQuery(id+"F6.wireOp",EDGE,"E20.0.10.0"),sQuery(id+"F6.wireOp",EDGE,"E20.0.11.0")])]}),"instanceName":"4"});
            var Q41;
            Q41=makeQuery(id+"F8.opPattern","COPY",BODY,{"derivedFrom":makeQuery(id+"F7.opExtrude","SWEPT_BODY",BODY,{"disambiguationData":[OSD([sQuery(id+"F6.wireOp",EDGE,"E15"),sQuery(id+"F6.wireOp",EDGE,"E16.MirrorCS"),sQuery(id+"F6.wireOp",EDGE,"E20.0.8.0"),sQuery(id+"F6.wireOp",EDGE,"E20.0.9.0")])]}),"instanceName":"4"});
            var Q42;
            Q42=makeQuery(id+"F8.opPattern","COPY",BODY,{"derivedFrom":makeQuery(id+"F7.opExtrude","SWEPT_BODY",BODY,{"disambiguationData":[OSD([sQuery(id+"F6.wireOp",EDGE,"E15"),sQuery(id+"F6.wireOp",EDGE,"E16.MirrorCS"),sQuery(id+"F6.wireOp",EDGE,"E20.0.6.0"),sQuery(id+"F6.wireOp",EDGE,"E20.0.7.0")])]}),"instanceName":"2"});
            var Q43;
            Q43=makeQuery(id+"F8.opPattern","COPY",BODY,{"derivedFrom":makeQuery(id+"F7.opExtrude","SWEPT_BODY",BODY,{"disambiguationData":[OSD([sQuery(id+"F6.wireOp",EDGE,"E15"),sQuery(id+"F6.wireOp",EDGE,"E16.MirrorCS"),sQuery(id+"F6.wireOp",EDGE,"E20.0.8.0"),sQuery(id+"F6.wireOp",EDGE,"E20.0.9.0")])]}),"instanceName":"2"});
            var Q44;
            Q44=makeQuery(id+"F8.opPattern","COPY",BODY,{"derivedFrom":makeQuery(id+"F7.opExtrude","SWEPT_BODY",BODY,{"disambiguationData":[OSD([sQuery(id+"F6.wireOp",EDGE,"E15"),sQuery(id+"F6.wireOp",EDGE,"E16.MirrorCS"),sQuery(id+"F6.wireOp",EDGE,"E20.0.10.0"),sQuery(id+"F6.wireOp",EDGE,"E20.0.11.0")])]}),"instanceName":"2"});
            var Q45;
            Q45=makeQuery(id+"F8.opPattern","COPY",BODY,{"derivedFrom":makeQuery(id+"F7.opExtrude","SWEPT_BODY",BODY,{"disambiguationData":[OSD([sQuery(id+"F6.wireOp",EDGE,"E15"),sQuery(id+"F6.wireOp",EDGE,"E16.MirrorCS"),sQuery(id+"F6.wireOp",EDGE,"E20.0.12.0"),sQuery(id+"F6.wireOp",EDGE,"E20.0.13.0")])]}),"instanceName":"2"});
            var Q46;
            Q46=makeQuery(id+"F8.opPattern","COPY",BODY,{"derivedFrom":makeQuery(id+"F7.opExtrude","SWEPT_BODY",BODY,{"disambiguationData":[OSD([sQuery(id+"F6.wireOp",EDGE,"E15"),sQuery(id+"F6.wireOp",EDGE,"E16.MirrorCS"),sQuery(id+"F6.wireOp",EDGE,"E20.0.14.0"),sQuery(id+"F6.wireOp",EDGE,"E20.0.15.0")])]}),"instanceName":"2"});
            var Q47;
            Q47=makeQuery(id+"F8.opPattern","COPY",BODY,{"derivedFrom":makeQuery(id+"F7.opExtrude","SWEPT_BODY",BODY,{"disambiguationData":[OSD([sQuery(id+"F6.wireOp",EDGE,"E15"),sQuery(id+"F6.wireOp",EDGE,"E16.MirrorCS"),sQuery(id+"F6.wireOp",EDGE,"E20.0.16.0"),sQuery(id+"F6.wireOp",EDGE,"E20.0.17.0")])]}),"instanceName":"2"});
            var Q48;
            Q48=makeQuery(id+"F8.opPattern","COPY",BODY,{"derivedFrom":makeQuery(id+"F7.opExtrude","SWEPT_BODY",BODY,{"disambiguationData":[OSD([sQuery(id+"F6.wireOp",EDGE,"E15"),sQuery(id+"F6.wireOp",EDGE,"E16.MirrorCS"),sQuery(id+"F6.wireOp",EDGE,"E19"),sQuery(id+"F6.wireOp",EDGE,"E20.0.1.0")])]}),"instanceName":"3"});
            var Q49;
            Q49=makeQuery(id+"F8.opPattern","COPY",BODY,{"derivedFrom":makeQuery(id+"F7.opExtrude","SWEPT_BODY",BODY,{"disambiguationData":[OSD([sQuery(id+"F6.wireOp",EDGE,"E15"),sQuery(id+"F6.wireOp",EDGE,"E16.MirrorCS"),sQuery(id+"F6.wireOp",EDGE,"E20.0.2.0"),sQuery(id+"F6.wireOp",EDGE,"E20.0.3.0")])]}),"instanceName":"3"});
            var Q50;
            Q50=makeQuery(id+"F8.opPattern","COPY",BODY,{"derivedFrom":makeQuery(id+"F7.opExtrude","SWEPT_BODY",BODY,{"disambiguationData":[OSD([sQuery(id+"F6.wireOp",EDGE,"E15"),sQuery(id+"F6.wireOp",EDGE,"E16.MirrorCS"),sQuery(id+"F6.wireOp",EDGE,"E20.0.4.0"),sQuery(id+"F6.wireOp",EDGE,"E20.0.5.0")])]}),"instanceName":"3"});
            var Q51;
            Q51=makeQuery(id+"F8.opPattern","COPY",BODY,{"derivedFrom":makeQuery(id+"F7.opExtrude","SWEPT_BODY",BODY,{"disambiguationData":[OSD([sQuery(id+"F6.wireOp",EDGE,"E15"),sQuery(id+"F6.wireOp",EDGE,"E16.MirrorCS"),sQuery(id+"F6.wireOp",EDGE,"E20.0.6.0"),sQuery(id+"F6.wireOp",EDGE,"E20.0.7.0")])]}),"instanceName":"3"});
            var Q52;
            Q52=makeQuery(id+"F8.opPattern","COPY",BODY,{"derivedFrom":makeQuery(id+"F7.opExtrude","SWEPT_BODY",BODY,{"disambiguationData":[OSD([sQuery(id+"F6.wireOp",EDGE,"E15"),sQuery(id+"F6.wireOp",EDGE,"E16.MirrorCS"),sQuery(id+"F6.wireOp",EDGE,"E20.0.8.0"),sQuery(id+"F6.wireOp",EDGE,"E20.0.9.0")])]}),"instanceName":"3"});
            var Q53;
            Q53=makeQuery(id+"F8.opPattern","COPY",BODY,{"derivedFrom":makeQuery(id+"F7.opExtrude","SWEPT_BODY",BODY,{"disambiguationData":[OSD([sQuery(id+"F6.wireOp",EDGE,"E15"),sQuery(id+"F6.wireOp",EDGE,"E16.MirrorCS"),sQuery(id+"F6.wireOp",EDGE,"E20.0.10.0"),sQuery(id+"F6.wireOp",EDGE,"E20.0.11.0")])]}),"instanceName":"3"});
            var Q54;
            Q54=makeQuery(id+"F8.opPattern","COPY",BODY,{"derivedFrom":makeQuery(id+"F7.opExtrude","SWEPT_BODY",BODY,{"disambiguationData":[OSD([sQuery(id+"F6.wireOp",EDGE,"E15"),sQuery(id+"F6.wireOp",EDGE,"E16.MirrorCS"),sQuery(id+"F6.wireOp",EDGE,"E20.0.12.0"),sQuery(id+"F6.wireOp",EDGE,"E20.0.13.0")])]}),"instanceName":"3"});
            var Q55;
            Q55=makeQuery(id+"F8.opPattern","COPY",BODY,{"derivedFrom":makeQuery(id+"F7.opExtrude","SWEPT_BODY",BODY,{"disambiguationData":[OSD([sQuery(id+"F6.wireOp",EDGE,"E15"),sQuery(id+"F6.wireOp",EDGE,"E16.MirrorCS"),sQuery(id+"F6.wireOp",EDGE,"E20.0.4.0"),sQuery(id+"F6.wireOp",EDGE,"E20.0.5.0")])]}),"instanceName":"4"});
            var Q56;
            Q56=makeQuery(id+"F8.opPattern","COPY",BODY,{"derivedFrom":makeQuery(id+"F7.opExtrude","SWEPT_BODY",BODY,{"disambiguationData":[OSD([sQuery(id+"F6.wireOp",EDGE,"E15"),sQuery(id+"F6.wireOp",EDGE,"E16.MirrorCS"),sQuery(id+"F6.wireOp",EDGE,"E20.0.6.0"),sQuery(id+"F6.wireOp",EDGE,"E20.0.7.0")])]}),"instanceName":"1"});
            var Q57;
            Q57=makeQuery(id+"F8.opPattern","COPY",BODY,{"derivedFrom":makeQuery(id+"F7.opExtrude","SWEPT_BODY",BODY,{"disambiguationData":[OSD([sQuery(id+"F6.wireOp",EDGE,"E15"),sQuery(id+"F6.wireOp",EDGE,"E16.MirrorCS"),sQuery(id+"F6.wireOp",EDGE,"E20.0.6.0"),sQuery(id+"F6.wireOp",EDGE,"E20.0.7.0")])]}),"instanceName":"4"});
            var Q58;
            Q58=makeQuery(id+"F8.opPattern","COPY",BODY,{"derivedFrom":makeQuery(id+"F7.opExtrude","SWEPT_BODY",BODY,{"disambiguationData":[OSD([sQuery(id+"F6.wireOp",EDGE,"E15"),sQuery(id+"F6.wireOp",EDGE,"E16.MirrorCS"),sQuery(id+"F6.wireOp",EDGE,"E20.0.2.0"),sQuery(id+"F6.wireOp",EDGE,"E20.0.3.0")])]}),"instanceName":"4"});
            var Q59;
            Q59=makeQuery(id+"F7.opExtrude","SWEPT_BODY",BODY,{"disambiguationData":[OSD([sQuery(id+"F6.wireOp",EDGE,"E15"),sQuery(id+"F6.wireOp",EDGE,"E16.MirrorCS"),sQuery(id+"F6.wireOp",EDGE,"E20.0.10.0"),sQuery(id+"F6.wireOp",EDGE,"E20.0.11.0")])]});
            var Q60;
            Q60=makeQuery(id+"F7.opExtrude","SWEPT_BODY",BODY,{"disambiguationData":[OSD([sQuery(id+"F6.wireOp",EDGE,"E15"),sQuery(id+"F6.wireOp",EDGE,"E16.MirrorCS"),sQuery(id+"F6.wireOp",EDGE,"E20.0.8.0"),sQuery(id+"F6.wireOp",EDGE,"E20.0.9.0")])]});
            var Q61;
            Q61=makeQuery(id+"F7.opExtrude","SWEPT_BODY",BODY,{"disambiguationData":[OSD([sQuery(id+"F6.wireOp",EDGE,"E15"),sQuery(id+"F6.wireOp",EDGE,"E16.MirrorCS"),sQuery(id+"F6.wireOp",EDGE,"E20.0.6.0"),sQuery(id+"F6.wireOp",EDGE,"E20.0.7.0")])]});
            var Q62;
            Q62=makeQuery(id+"F7.opExtrude","SWEPT_BODY",BODY,{"disambiguationData":[OSD([sQuery(id+"F6.wireOp",EDGE,"E15"),sQuery(id+"F6.wireOp",EDGE,"E16.MirrorCS"),sQuery(id+"F6.wireOp",EDGE,"E19"),sQuery(id+"F6.wireOp",EDGE,"E20.0.1.0")])]});
            var Q63;
            Q63=makeQuery(id+"F7.opExtrude","SWEPT_BODY",BODY,{"disambiguationData":[OSD([sQuery(id+"F6.wireOp",EDGE,"E15"),sQuery(id+"F6.wireOp",EDGE,"E16.MirrorCS"),sQuery(id+"F6.wireOp",EDGE,"E20.0.4.0"),sQuery(id+"F6.wireOp",EDGE,"E20.0.5.0")])]});
            var Q64;
            Q64=makeQuery(id+"F8.opPattern","COPY",BODY,{"derivedFrom":makeQuery(id+"F7.opExtrude","SWEPT_BODY",BODY,{"disambiguationData":[OSD([sQuery(id+"F6.wireOp",EDGE,"E15"),sQuery(id+"F6.wireOp",EDGE,"E16.MirrorCS"),sQuery(id+"F6.wireOp",EDGE,"E20.0.14.0"),sQuery(id+"F6.wireOp",EDGE,"E20.0.15.0")])]}),"instanceName":"7"});
            var Q65;
            Q65=makeQuery(id+"F8.opPattern","COPY",BODY,{"derivedFrom":makeQuery(id+"F7.opExtrude","SWEPT_BODY",BODY,{"disambiguationData":[OSD([sQuery(id+"F6.wireOp",EDGE,"E15"),sQuery(id+"F6.wireOp",EDGE,"E16.MirrorCS"),sQuery(id+"F6.wireOp",EDGE,"E20.0.12.0"),sQuery(id+"F6.wireOp",EDGE,"E20.0.13.0")])]}),"instanceName":"7"});
            var Q66;
            Q66=makeQuery(id+"F8.opPattern","COPY",BODY,{"derivedFrom":makeQuery(id+"F7.opExtrude","SWEPT_BODY",BODY,{"disambiguationData":[OSD([sQuery(id+"F6.wireOp",EDGE,"E15"),sQuery(id+"F6.wireOp",EDGE,"E16.MirrorCS"),sQuery(id+"F6.wireOp",EDGE,"E20.0.14.0"),sQuery(id+"F6.wireOp",EDGE,"E20.0.15.0")])]}),"instanceName":"3"});
            var Q67;
            Q67=makeQuery(id+"F8.opPattern","COPY",BODY,{"derivedFrom":makeQuery(id+"F7.opExtrude","SWEPT_BODY",BODY,{"disambiguationData":[OSD([sQuery(id+"F6.wireOp",EDGE,"E15"),sQuery(id+"F6.wireOp",EDGE,"E16.MirrorCS"),sQuery(id+"F6.wireOp",EDGE,"E20.0.10.0"),sQuery(id+"F6.wireOp",EDGE,"E20.0.11.0")])]}),"instanceName":"7"});
            var Q68;
            Q68=makeQuery(id+"F8.opPattern","COPY",BODY,{"derivedFrom":makeQuery(id+"F7.opExtrude","SWEPT_BODY",BODY,{"disambiguationData":[OSD([sQuery(id+"F6.wireOp",EDGE,"E15"),sQuery(id+"F6.wireOp",EDGE,"E16.MirrorCS"),sQuery(id+"F6.wireOp",EDGE,"E20.0.2.0"),sQuery(id+"F6.wireOp",EDGE,"E20.0.3.0")])]}),"instanceName":"7"});
            var Q69;
            Q69=makeQuery(id+"F8.opPattern","COPY",BODY,{"derivedFrom":makeQuery(id+"F7.opExtrude","SWEPT_BODY",BODY,{"disambiguationData":[OSD([sQuery(id+"F6.wireOp",EDGE,"E15"),sQuery(id+"F6.wireOp",EDGE,"E16.MirrorCS"),sQuery(id+"F6.wireOp",EDGE,"E20.0.16.0"),sQuery(id+"F6.wireOp",EDGE,"E20.0.17.0")])]}),"instanceName":"3"});
            var Q70;
            Q70=makeQuery(id+"F8.opPattern","COPY",BODY,{"derivedFrom":makeQuery(id+"F7.opExtrude","SWEPT_BODY",BODY,{"disambiguationData":[OSD([sQuery(id+"F6.wireOp",EDGE,"E15"),sQuery(id+"F6.wireOp",EDGE,"E16.MirrorCS"),sQuery(id+"F6.wireOp",EDGE,"E19"),sQuery(id+"F6.wireOp",EDGE,"E20.0.1.0")])]}),"instanceName":"4"});
            var Q71;
            Q71=makeQuery(id+"F8.opPattern","COPY",BODY,{"derivedFrom":makeQuery(id+"F7.opExtrude","SWEPT_BODY",BODY,{"disambiguationData":[OSD([sQuery(id+"F6.wireOp",EDGE,"E15"),sQuery(id+"F6.wireOp",EDGE,"E16.MirrorCS"),sQuery(id+"F6.wireOp",EDGE,"E20.0.8.0"),sQuery(id+"F6.wireOp",EDGE,"E20.0.9.0")])]}),"instanceName":"7"});
            var Q72;
            Q72=makeQuery(id+"F4.opRevolve","SWEPT_BODY",BODY,{"disambiguationData":[OSD([sQuery(id+"F3.wireOp",EDGE,"E8"),sQuery(id+"F3.wireOp",EDGE,"E9"),sQuery(id+"F3.wireOp",EDGE,"E10"),sQuery(id+"F3.wireOp",EDGE,"E11")])]});
            booleanBodies(context, id + "F9", {"operationType" : BooleanOperationType.SUBTRACTION, "tools" : qUnion([Q0, Q1, Q2, Q3, Q4, Q5, Q6, Q7, Q8, Q9, Q10, Q11, Q12, Q13, Q14, Q15, Q16, Q17, Q18, Q19, Q20, Q21, Q22, Q23, Q24, Q25, Q26, Q27, Q28, Q29, Q30, Q31, Q32, Q33, Q34, Q35, Q36, Q37, Q38, Q39, Q40, Q41, Q42, Q43, Q44, Q45, Q46, Q47, Q48, Q49, Q50, Q51, Q52, Q53, Q54, Q55, Q56, Q57, Q58, Q59, Q60, Q61, Q62, Q63, Q64, Q65, Q66, Q67, Q68, Q69, Q70, Q71]), "targets" : qUnion([Q72])});
        }
        {
            var Q0;
            Q0=makeQuery(id+"F4.opRevolve","SWEPT_EDGE",EDGE,{"disambiguationData":[OSD([sQuery(id+"F3.wireOp",EDGE,"E8"),sQuery(id+"F3.wireOp",EDGE,"E9")])]});
            fillet(context, id + "F10", {"entities" : qUnion([Q0]), "radius" : 3 * mm, "tangentPropagation" : true, "allowEdgeOverflow" : false});
        }
        {
            var Q0;
            Q0=makeQuery(id+"F1.opExtrude","CAP_EDGE",EDGE,{"disambiguationData":[OSD([sQuery(id+"F0.wireOp",EDGE,"E7")])],"isStart":true});
            chamfer(context, id + "F11", {"entities" : qUnion([Q0]), "width" : 1.1 * mm, "tangentPropagation" : true});
        }
    });
